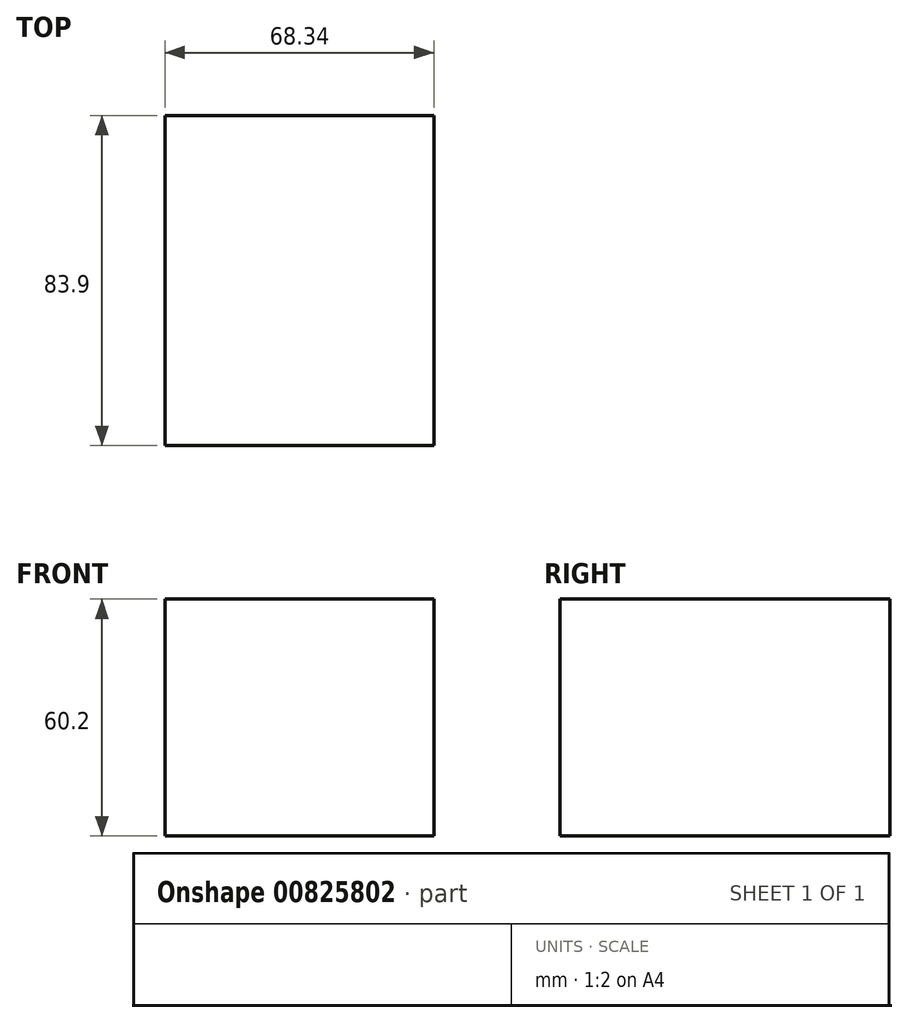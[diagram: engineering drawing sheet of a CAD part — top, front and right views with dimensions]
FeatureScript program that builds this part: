
annotation { "Feature Type Name" : "Feature", "Feature Type Description" : "" }
export const myFeature = defineFeature(function(context is Context, id is Id, definition is map)
    precondition{}
    {
        {
            var Q0;
            Q0=qCreatedBy(makeId("Top.planeOp"),FACE);
            var sketch = newSketch(context, id + "F0", { "sketchPlane" : qUnion([Q0])});
            skLineSegment(sketch, "E0.bottom", {"start": v(-39.36, 38.58) * mm, "end": v(28.98, 38.58) * mm});
            skLineSegment(sketch, "E0.top", {"start": v(-39.36, -45.32) * mm, "end": v(28.98, -45.32) * mm});
            skLineSegment(sketch, "E0.left", {"start": v(-39.36, 38.58) * mm, "end": v(-39.36, -45.32) * mm});
            skLineSegment(sketch, "E0.right", {"start": v(28.98, 38.58) * mm, "end": v(28.98, -45.32) * mm});
            skSolve(sketch);
        }
        {
            var Q0;
            Q0=makeQuery(id+"F0.imprint","IMPRINT",FACE,{"disambiguationData":[TD([[makeQuery(id+"F0.imprint","IMPRINT",EDGE,{"derivedFrom":sQuery(id+"F0.wireOp",EDGE,"E0.bottom")}),-1.0]])]});
            extrude(context, id + "F1", {"entities" : qUnion([Q0]), "depth" : 60.2 * mm, "offsetDistance" : 25 * mm});
        }
    });
